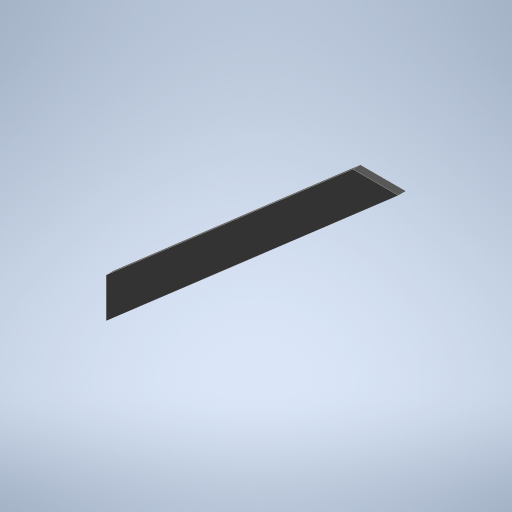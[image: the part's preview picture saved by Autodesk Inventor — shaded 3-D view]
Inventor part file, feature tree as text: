
AUTODESK INVENTOR PART (.ipt)
format: ipt  version: 2024.3 (Build 283343000, 343)  size: 279,040 bytes
history: native  units: mm
features: extrude x3, sketch x3, projected_geometry x2, other x1, fillet x1
ambient origin geometry x8: Origin, YZ Plane, XZ Plane, XY Plane, X Axis, Y Axis, Z Axis, Center Point
bodies: Body1 (feature_tree)
feature tree (10):
  other  "ソリッド1"
  extrude  "押し出し1"  Depth=195.0mm
  extrude  "押し出し11"  Depth=170.0mm
  fillet  "フィレット7"  Radius=5.0mm
  extrude  "押し出し12"  Depth=20.0mm
  sketch  "スケッチ1"
  sketch  "スケッチ13"
  projected_geometry  "投影ループ6"
  sketch  "スケッチ14"
  projected_geometry  "投影ループ7"
